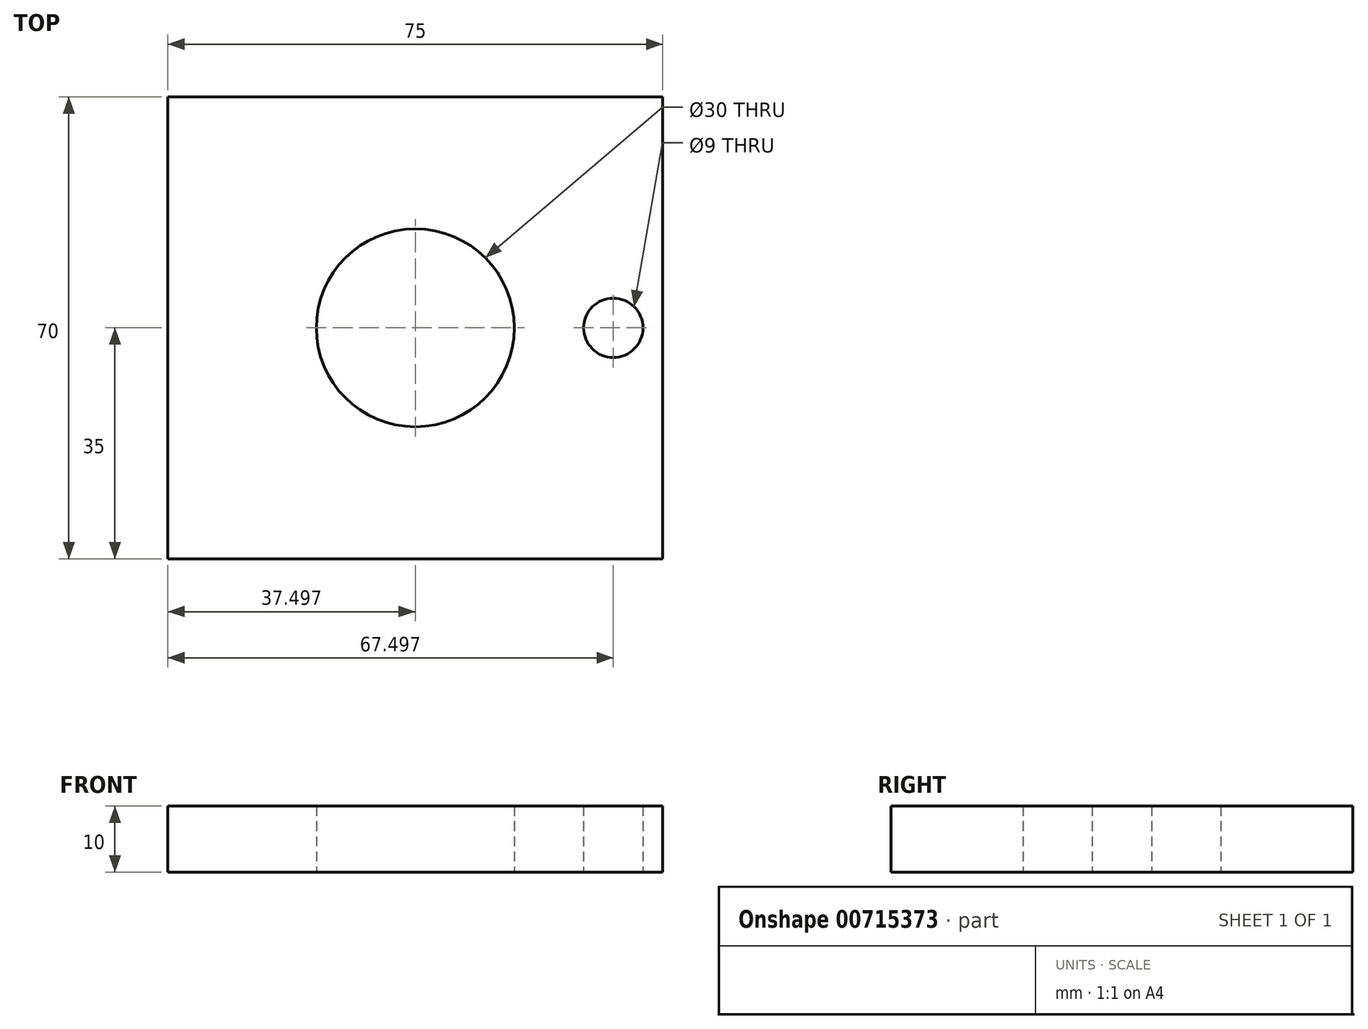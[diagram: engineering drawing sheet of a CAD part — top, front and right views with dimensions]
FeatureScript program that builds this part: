
annotation { "Feature Type Name" : "Feature", "Feature Type Description" : "" }
export const myFeature = defineFeature(function(context is Context, id is Id, definition is map)
    precondition{}
    {
        {
            var Q0;
            Q0=qCreatedBy(makeId("Top.planeOp"),FACE);
            var sketch = newSketch(context, id + "F0", { "sketchPlane" : qUnion([Q0])});
            skLineSegment(sketch, "E0.bottom", {"start": v(-32.78, 35) * mm, "end": v(42.22, 35) * mm});
            skLineSegment(sketch, "E0.top", {"start": v(-32.78, -35) * mm, "end": v(42.22, -35) * mm});
            skLineSegment(sketch, "E0.left", {"start": v(-32.78, 35) * mm, "end": v(-32.78, -35) * mm});
            skLineSegment(sketch, "E0.right", {"start": v(42.22, 35) * mm, "end": v(42.22, -35) * mm});
            skLineSegment(sketch, "E1", {"start": v(-32.78, 0) * mm, "end": v(42.22, 0) * mm, "construction": true});
            skPoint(sketch, "E1.endSnap0", {"position": v(42.22, 0) * mm});
            skCircle(sketch, "E2", {"center": v(4.72, 0) * mm, "radius": 15 * mm});
            skCircle(sketch, "E3", {"center": v(34.72, 0) * mm, "radius": 4.5 * mm});
            skSolve(sketch);
        }
        {
            var Q0;
            Q0=makeQuery(id+"F0.imprint","IMPRINT",FACE,{"disambiguationData":[TD([[makeQuery(id+"F0.imprint","IMPRINT",EDGE,{"derivedFrom":sQuery(id+"F0.wireOp",EDGE,"E0.bottom")}),-1.0]])]});
            extrude(context, id + "F1", {"entities" : qUnion([Q0]), "depth" : 10 * mm, "offsetDistance" : 25.4 * mm});
        }
    });
